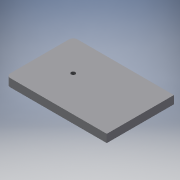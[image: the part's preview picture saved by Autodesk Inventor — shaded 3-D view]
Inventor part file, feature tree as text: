
AUTODESK INVENTOR PART (.ipt)
format: ipt  version: 2018 (Build 220112000, 112)  size: 113,152 bytes
history: native  units: mm
features: other x6, extrude x1, hole x1, fillet x1, sketch x1
ambient origin geometry x8: Origin, YZ Plane, XZ Plane, XY Plane, X Axis, Y Axis, Z Axis, Center Point
bodies: Body1 (feature_tree)
feature tree (10):
  other  "Sólido1"
  extrude  "Extrusão1"  Depth=120.0mm
  hole  "Furo2"  [1 undecoded]
  fillet  "Arredondamento3"  Radius=9.52mm
  sketch  "Esboço1"  dims[d0=120.0mm d1=120.0mm d2=80.0mm d3=9.52mm d4=0.0mm d95=6.0mm d96=4.917mm d97=12.0mm d98=4.0mm d99=2.0mm d100=90.0deg d101=17.1mm d102=20.594885mm d103=5.0mm d104=37.5mm]
  other  "Referência1"
  other  "Referência2"
  other  "<userpath>\Documents\OpenCNC\MONTAGEM\CNC1.iam"
  other  "CNC1.iam"
  other  "PERFIL_ESTRUTURAL_40X80_EIXO_Y:1"
note: 1 required parameter value undecoded (feature->parameter linkage not recoverable at this tier; creation-order binding heuristic only, values carry confidence <= 0.55)
